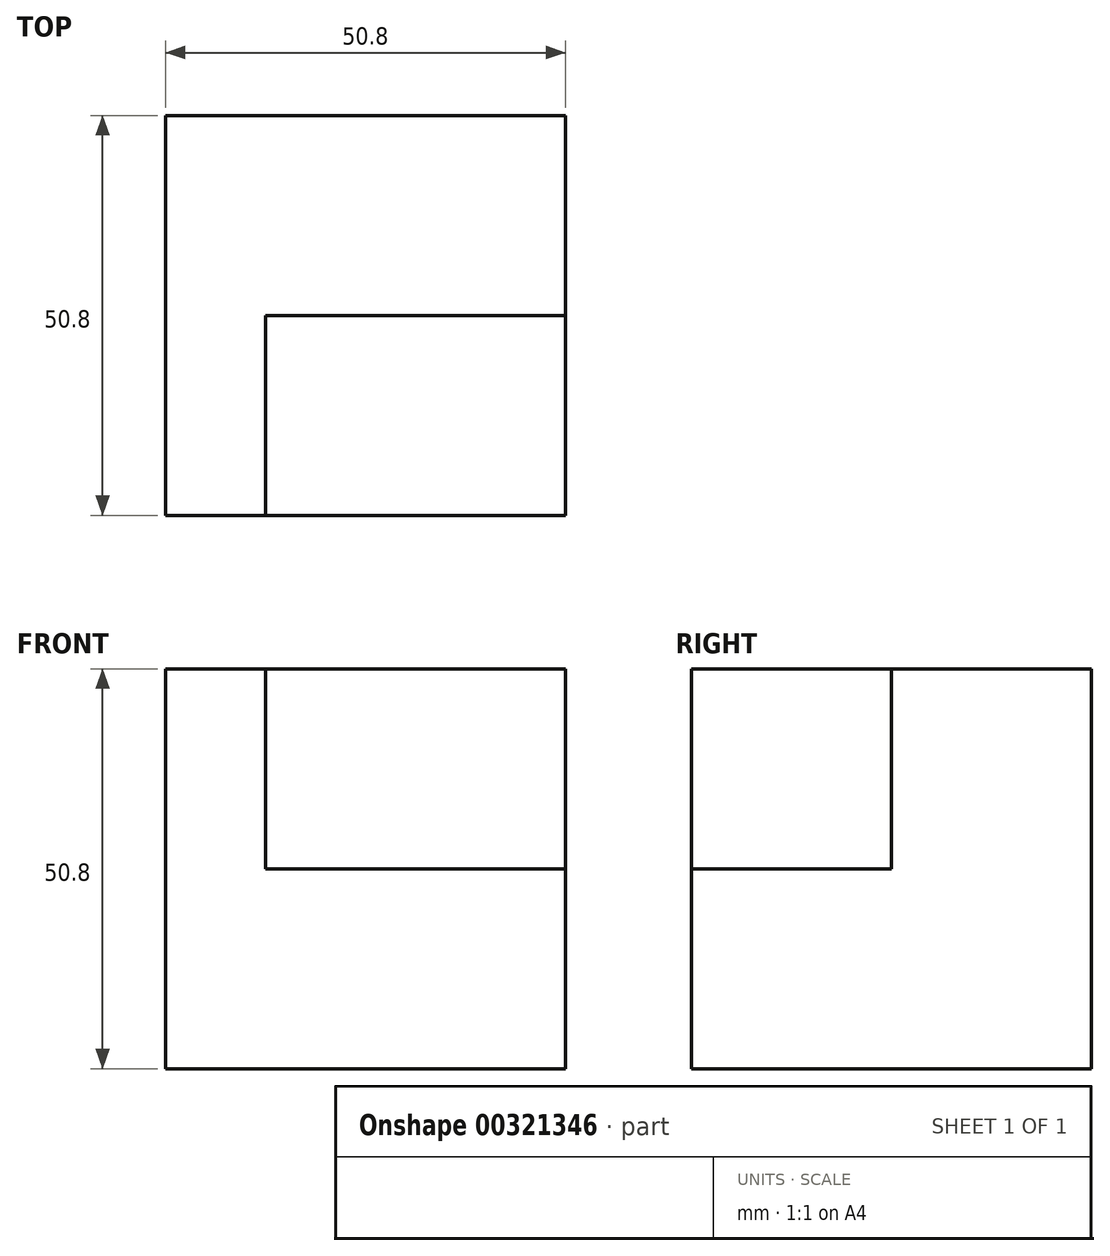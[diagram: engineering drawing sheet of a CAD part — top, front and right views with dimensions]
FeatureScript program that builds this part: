
annotation { "Feature Type Name" : "Feature", "Feature Type Description" : "" }
export const myFeature = defineFeature(function(context is Context, id is Id, definition is map)
    precondition{}
    {
        {
            var Q0;
            Q0=qCreatedBy(makeId("Front.planeOp"),FACE);
            var sketch = newSketch(context, id + "F0", { "sketchPlane" : qUnion([Q0])});
            skLineSegment(sketch, "E0.bottom", {"start": v(-25.4, 21.38) * mm, "end": v(25.4, 21.38) * mm});
            skLineSegment(sketch, "E0.top", {"start": v(-25.4, -29.42) * mm, "end": v(25.4, -29.42) * mm});
            skLineSegment(sketch, "E0.left", {"start": v(-25.4, 21.38) * mm, "end": v(-25.4, -29.42) * mm});
            skLineSegment(sketch, "E0.right", {"start": v(25.4, 21.38) * mm, "end": v(25.4, -29.42) * mm});
            skSolve(sketch);
        }
        {
            var Q0;
            Q0=makeQuery(id+"F0.imprint","IMPRINT",FACE,{"disambiguationData":[TD([[makeQuery(id+"F0.imprint","IMPRINT",EDGE,{"derivedFrom":sQuery(id+"F0.wireOp",EDGE,"E0.bottom")}),-1.0]])]});
            extrude(context, id + "F1", {"entities" : qUnion([Q0]), "depth" : 50.8 * mm});
        }
        {
            var Q0;
            Q0=makeQuery(id+"F1.opExtrude","SWEPT_FACE",FACE,{"disambiguationData":[OSD([sQuery(id+"F0.wireOp",EDGE,"E0.bottom")])]});
            var sketch = newSketch(context, id + "F2", { "sketchPlane" : qUnion([Q0])});
            skLineSegment(sketch, "E1", {"start": v(25.4, -25.4) * mm, "end": v(-12.7, -25.4) * mm});
            skLineSegment(sketch, "E2", {"start": v(-12.7, -25.4) * mm, "end": v(-12.7, -50.8) * mm});
            skLineSegment(sketch, "E3", {"start": v(-12.7, -50.8) * mm, "end": v(25.4, -50.8) * mm});
            skLineSegment(sketch, "E4", {"start": v(25.4, -50.8) * mm, "end": v(25.4, -25.4) * mm});
            skSolve(sketch);
        }
        {
            var Q0;
            Q0=makeQuery(id+"F2.imprint","IMPRINT",FACE,{"disambiguationData":[TD([[makeQuery(id+"F2.imprint","IMPRINT",EDGE,{"derivedFrom":sQuery(id+"F2.wireOp",EDGE,"E1")}),1.0]])]});
            extrude(context, id + "F3", {"entities" : qUnion([Q0]), "operationType" : NewBodyOperationType.REMOVE, "oppositeDirection" : true, "depth" : 25.4 * mm});
        }
    });
